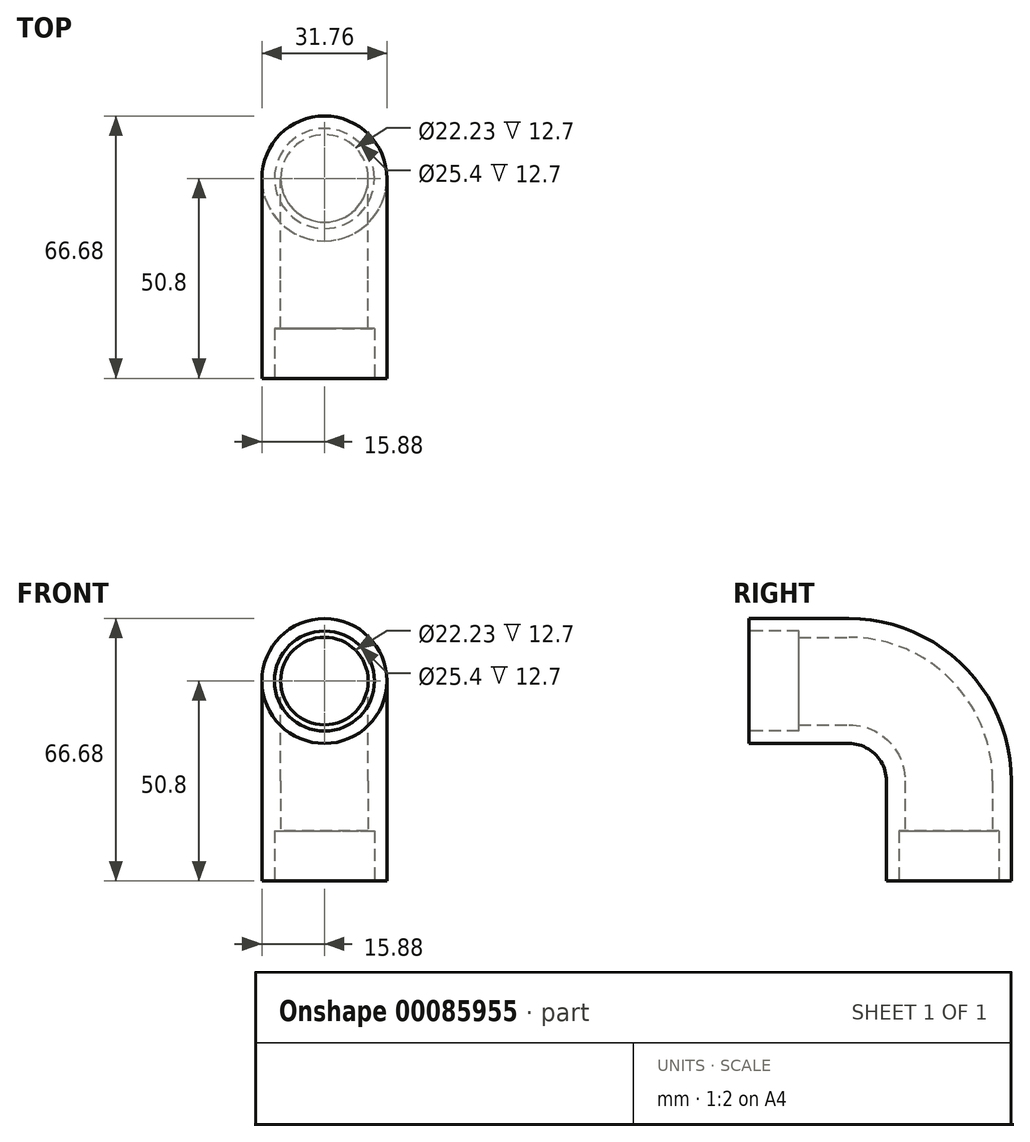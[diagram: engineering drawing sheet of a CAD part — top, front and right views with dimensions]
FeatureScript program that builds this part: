
annotation { "Feature Type Name" : "Feature", "Feature Type Description" : "" }
export const myFeature = defineFeature(function(context is Context, id is Id, definition is map)
    precondition{}
    {
        {
            var Q0;
            Q0=qCreatedBy(makeId("Front.planeOp"),FACE);
            var sketch = newSketch(context, id + "F0", { "sketchPlane" : qUnion([Q0])});
            skCircle(sketch, "E0", {"center": v(0, 0) * mm, "radius": 11.11 * mm});
            skCircle(sketch, "E1", {"center": v(0, 0) * mm, "radius": 15.88 * mm});
            skSolve(sketch);
        }
        {
            var Q0;
            Q0=qCreatedBy(makeId("Right.planeOp"),FACE);
            var sketch = newSketch(context, id + "F1", { "sketchPlane" : qUnion([Q0])});
            skLineSegment(sketch, "E2", {"start": v(0, 0) * mm, "end": v(25.4, 0) * mm});
            skLineSegment(sketch, "E3", {"start": v(50.8, -25.4) * mm, "end": v(50.8, -50.8) * mm});
            skPoint(sketch, "E4.visualSharp", {"position": v(50.8, 0) * mm});
            skArc(sketch, "E4.filletArc", {"start": v(50.8, -25.4) * mm, "mid": v(43.36, -7.44) * mm, "end": v(25.4, 0) * mm});
            skSolve(sketch);
        }
        {
            var Q0;
            Q0=makeQuery(id+"F0.imprint","IMPRINT",FACE,{"disambiguationData":[TD([[makeQuery(id+"F0.imprint","IMPRINT",EDGE,{"derivedFrom":sQuery(id+"F0.wireOp",EDGE,"E0")}),-1.0]])]});
            var Q1;
            Q1=sQuery(id+"F1.wireOp",EDGE,"E2");
            var Q2;
            Q2=sQuery(id+"F1.wireOp",EDGE,"E4.filletArc");
            var Q3;
            Q3=sQuery(id+"F1.wireOp",EDGE,"E3");
            sweep(context, id + "F2", {"profiles" : qUnion([Q0]), "path" : qUnion([Q1, Q2, Q3])});
        }
        {
            var Q0;
            Q0=makeQuery(id+"F2.opSweep","CAP_FACE",FACE,{"disambiguationData":[OSD([sQuery(id+"F0.wireOp",EDGE,"E0"),sQuery(id+"F0.wireOp",EDGE,"E1"),sQuery(id+"F1.wireOp",VERTEX,"E2.start")])],"isStart":true});
            var sketch = newSketch(context, id + "F3", { "sketchPlane" : qUnion([Q0])});
            skCircle(sketch, "E5", {"center": v(0, 0) * mm, "radius": 12.7 * mm});
            skSolve(sketch);
        }
        {
            var Q0;
            Q0=makeQuery(id+"F3.imprint","IMPRINT",FACE,{"disambiguationData":[TD([[makeQuery(id+"F3.imprint","IMPRINT",EDGE,{"derivedFrom":sQuery(id+"F3.wireOp",EDGE,"E5")}),1.0]])]});
            extrude(context, id + "F4", {"entities" : qUnion([Q0]), "operationType" : NewBodyOperationType.REMOVE, "oppositeDirection" : true, "depth" : 12.7 * mm});
        }
        {
            var Q0;
            Q0=makeQuery(id+"F2.opSweep","CAP_FACE",FACE,{"disambiguationData":[OSD([sQuery(id+"F0.wireOp",EDGE,"E0"),sQuery(id+"F0.wireOp",EDGE,"E1"),sQuery(id+"F1.wireOp",VERTEX,"E3.end")])],"isStart":false});
            var sketch = newSketch(context, id + "F5", { "sketchPlane" : qUnion([Q0])});
            skCircle(sketch, "E6", {"center": v(0, -50.8) * mm, "radius": 12.7 * mm});
            skSolve(sketch);
        }
        {
            var Q0;
            Q0=makeQuery(id+"F5.imprint","IMPRINT",FACE,{"disambiguationData":[TD([[makeQuery(id+"F5.imprint","IMPRINT",EDGE,{"derivedFrom":sQuery(id+"F5.wireOp",EDGE,"E6")}),1.0]])]});
            extrude(context, id + "F6", {"entities" : qUnion([Q0]), "operationType" : NewBodyOperationType.REMOVE, "oppositeDirection" : true, "depth" : 12.7 * mm});
        }
    });
